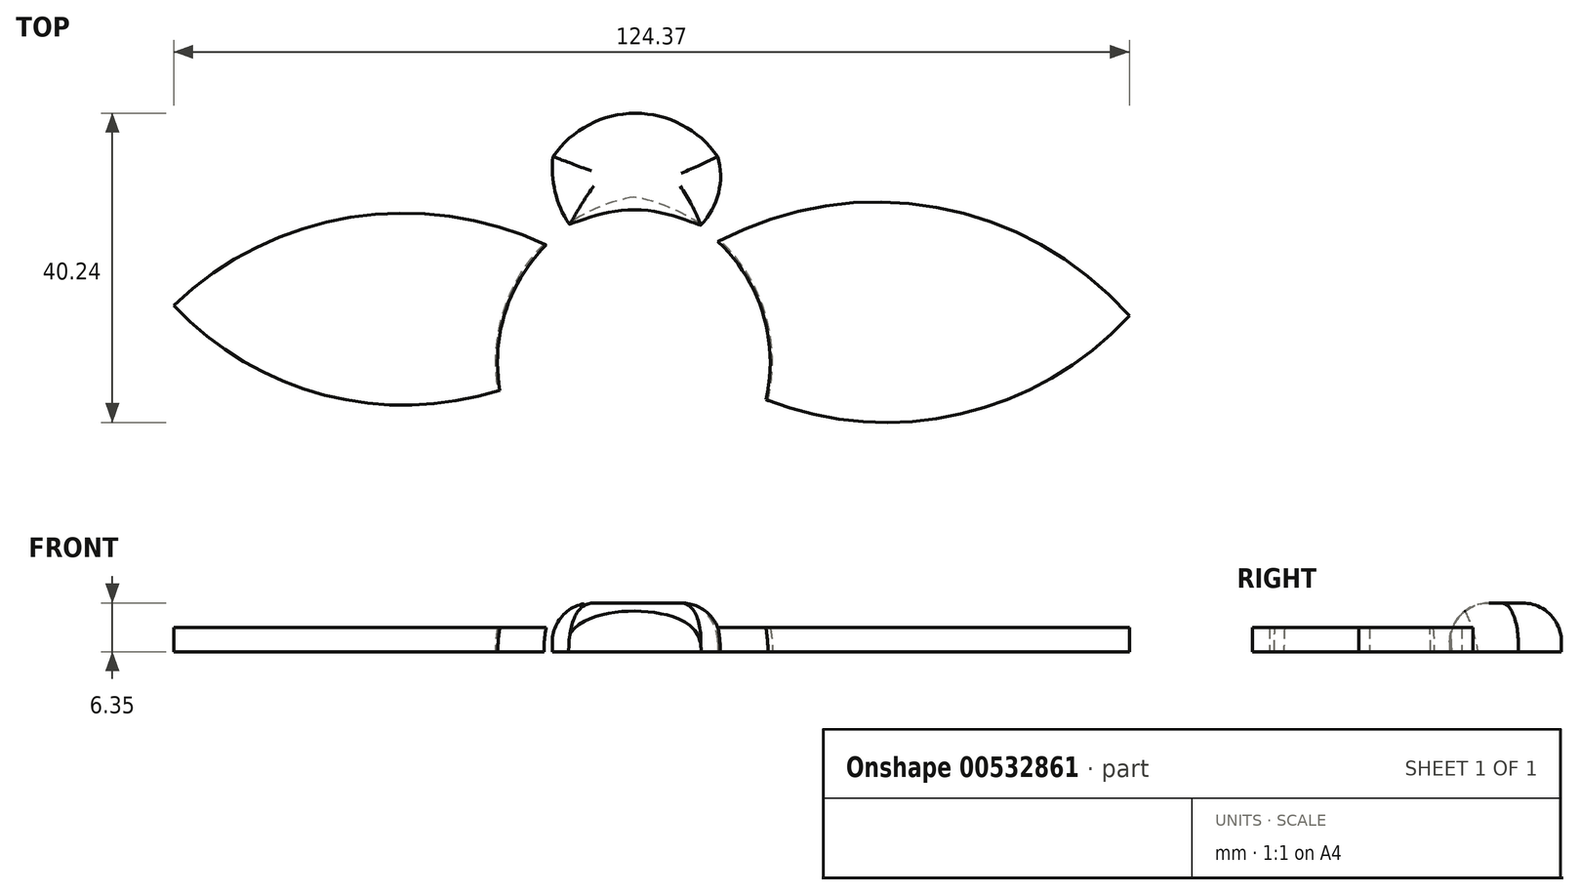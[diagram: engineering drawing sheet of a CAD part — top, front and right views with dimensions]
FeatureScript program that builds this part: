
annotation { "Feature Type Name" : "Feature", "Feature Type Description" : "" }
export const myFeature = defineFeature(function(context is Context, id is Id, definition is map)
    precondition{}
    {
        {
            var Q0;
            Q0=qCreatedBy(makeId("Top.planeOp"),FACE);
            var sketch = newSketch(context, id + "F0", { "sketchPlane" : qUnion([Q0])});
            skArc(sketch, "E0", {"start": v(0, -42.3) * mm, "mid": v(21.92, -2.6) * mm, "end": v(0, 37.13) * mm});
            skLineSegment(sketch, "E1", {"start": v(0, 49.5) * mm, "end": v(0, -54.68) * mm, "construction": true});
            skSolve(sketch);
        }
        {
            var Q0;
            Q0=sQuery(id+"F0.wireOp",EDGE,"E0");
            var Q1;
            Q1=sQuery(id+"F0.wireOp",EDGE,"E1");
            revolve(context, id + "F1", {"bodyType" : ToolBodyType.SURFACE, "surfaceEntities" : qUnion([Q0]), "axis" : qUnion([Q1]), "revolveType" : RevolveType.FULL});
        }
        {
            var Q0;
            Q0=qCreatedBy(makeId("Right.planeOp"),FACE);
            var sketch = newSketch(context, id + "F2", { "sketchPlane" : qUnion([Q0])});
            skArc(sketch, "E2", {"start": v(17.69, 0) * mm, "mid": v(39.16, -18.04) * mm, "end": v(60.64, 0) * mm});
            skLineSegment(sketch, "E3", {"start": v(17.69, 0) * mm, "end": v(60.64, 0) * mm});
            skSolve(sketch);
        }
        {
            var Q0;
            Q0 = qSketchRegion(id + "F2", true);
            var Q1;
            Q1=sQuery(id+"F2.wireOp",EDGE,"E3");
            revolve(context, id + "F3", {"entities" : qUnion([Q0]), "axis" : qUnion([Q1]), "revolveType" : RevolveType.FULL});
        }
        {
            var Q0;
            Q0=qCreatedBy(makeId("Top.planeOp"),FACE);
            var sketch = newSketch(context, id + "F4", { "sketchPlane" : qUnion([Q0])});
            skArc(sketch, "E4", {"start": v(64.5, 45.18) * mm, "mid": v(32.55, 59.98) * mm, "end": v(0, 46.54) * mm});
            skArc(sketch, "E5", {"start": v(0, 46.54) * mm, "mid": v(31.94, 31.31) * mm, "end": v(64.5, 45.18) * mm});
            skArc(sketch, "E6", {"start": v(0, 46.54) * mm, "mid": v(-29.94, 58.55) * mm, "end": v(-59.87, 46.54) * mm});
            skArc(sketch, "E7", {"start": v(-59.87, 46.54) * mm, "mid": v(-29.94, 33.55) * mm, "end": v(0, 46.54) * mm});
            skSolve(sketch);
        }
        {
            var Q0;
            Q0 = qSketchRegion(id + "F4", true);
            extrude(context, id + "F5", {"entities" : qUnion([Q0]), "operationType" : NewBodyOperationType.ADD, "depth" : 3.17 * mm, "offsetDistance" : 25.4 * mm});
        }
        {
            var Q0;
            Q0=qCreatedBy(makeId("Top.planeOp"),FACE);
            var sketch = newSketch(context, id + "F6", { "sketchPlane" : qUnion([Q0])});
            skArc(sketch, "E8", {"start": v(-10.52, 65.9) * mm, "mid": v(-10.24, 61.26) * mm, "end": v(-8.34, 57) * mm});
            skArc(sketch, "E9", {"start": v(10.9, 65.9) * mm, "mid": v(0.2, 71.54) * mm, "end": v(-10.52, 65.9) * mm});
            skArc(sketch, "E10", {"start": v(8.73, 57) * mm, "mid": v(11.02, 61.16) * mm, "end": v(10.9, 65.9) * mm});
            skLineSegment(sketch, "E11", {"start": v(-8.34, 57) * mm, "end": v(8.73, 57) * mm});
            skSolve(sketch);
        }
        {
            var Q0;
            Q0 = qSketchRegion(id + "F6", true);
            extrude(context, id + "F7", {"entities" : qUnion([Q0]), "operationType" : NewBodyOperationType.ADD, "depth" : 6.35 * mm, "offsetDistance" : 25.4 * mm});
        }
        {
            var Q0;
            Q0=makeQuery(id+"F7.opExtrude","CAP_FACE",FACE,{"disambiguationData":[OSD([sQuery(id+"F6.wireOp",EDGE,"E8"),sQuery(id+"F6.wireOp",EDGE,"E9"),sQuery(id+"F6.wireOp",EDGE,"E10"),sQuery(id+"F6.wireOp",EDGE,"E11")])],"isStart":false});
            fillet(context, id + "F8", {"entities" : qUnion([Q0]), "radius" : 5.08 * mm, "tangentPropagation" : true, "allowEdgeOverflow" : false});
        }
    });
